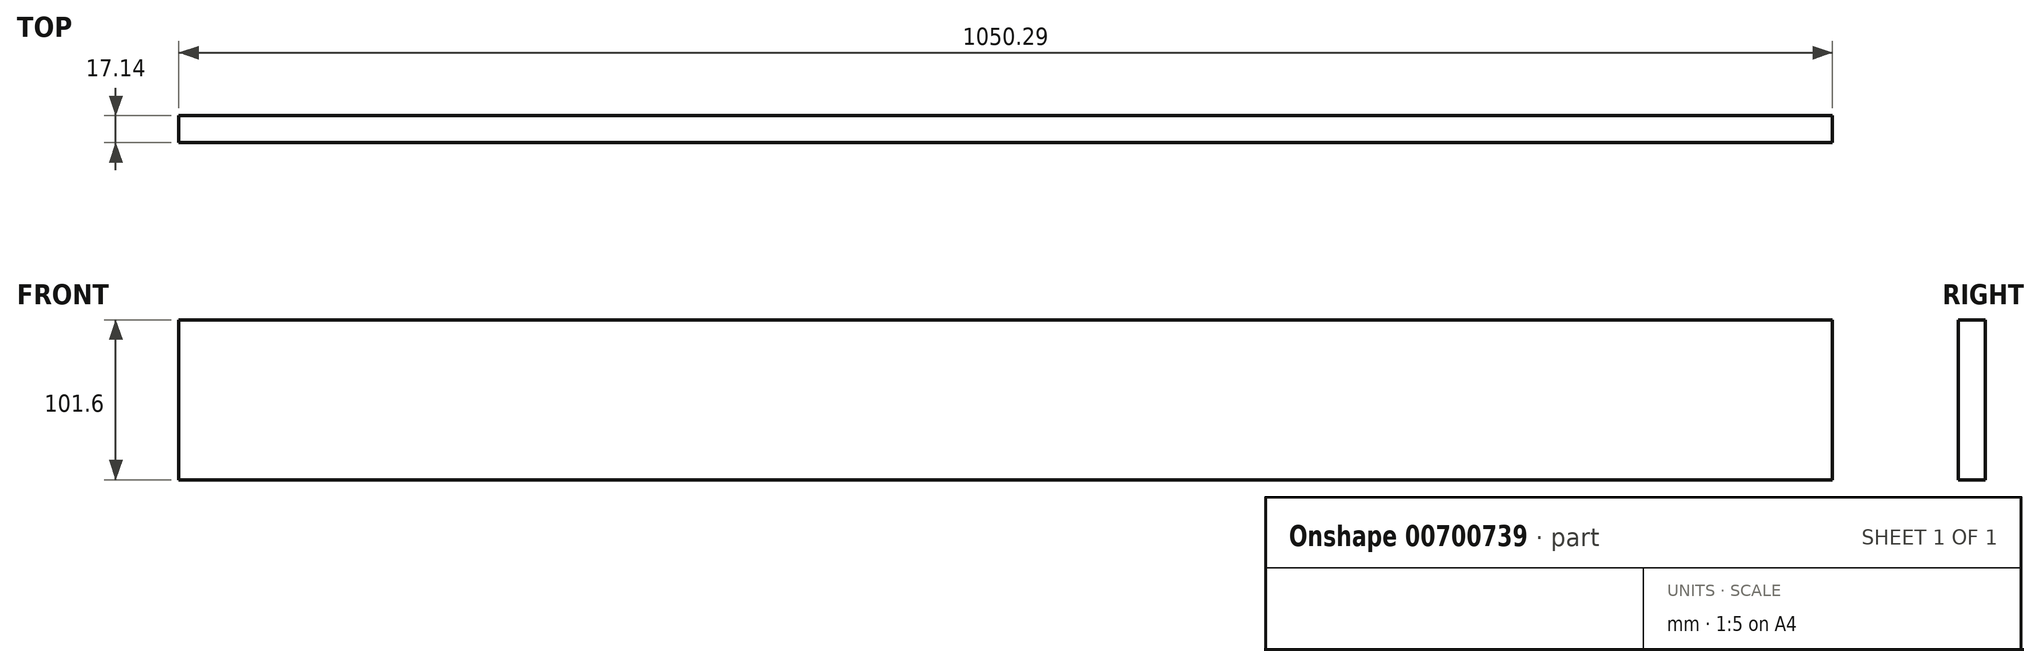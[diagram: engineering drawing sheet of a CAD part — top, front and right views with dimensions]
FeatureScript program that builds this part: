
annotation { "Feature Type Name" : "Feature", "Feature Type Description" : "" }
export const myFeature = defineFeature(function(context is Context, id is Id, definition is map)
    precondition{}
    {
        {
            var Q0;
            Q0=qCreatedBy(makeId("Front.planeOp"),FACE);
            var sketch = newSketch(context, id + "F0", { "sketchPlane" : qUnion([Q0])});
            skLineSegment(sketch, "E0.bottom", {"start": v(0, 0) * mm, "end": v(1050.29, 0) * mm});
            skLineSegment(sketch, "E0.top", {"start": v(0, 101.6) * mm, "end": v(1050.3, 101.6) * mm});
            skLineSegment(sketch, "E0.left", {"start": v(0, 0) * mm, "end": v(0, 101.6) * mm});
            skLineSegment(sketch, "E0.right", {"start": v(1050.3, 0) * mm, "end": v(1050.3, 101.6) * mm});
            skSolve(sketch);
        }
        {
            var Q0;
            Q0 = qSketchRegion(id + "F0", true);
            extrude(context, id + "F1", {"entities" : qUnion([Q0]), "depth" : 17.14 * mm, "offsetDistance" : 25.4 * mm});
        }
    });
